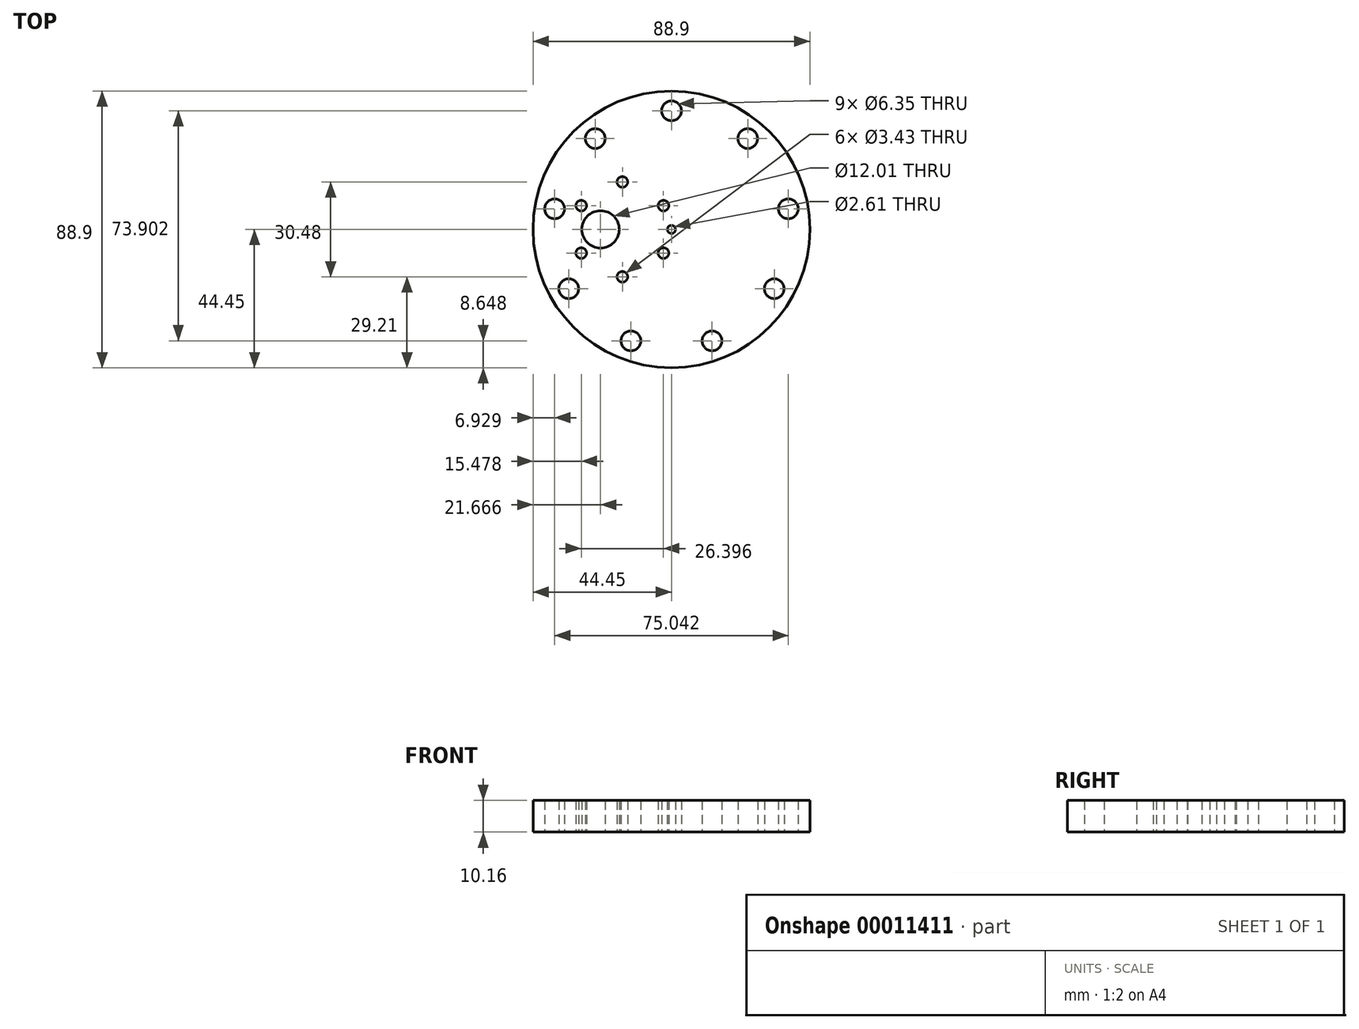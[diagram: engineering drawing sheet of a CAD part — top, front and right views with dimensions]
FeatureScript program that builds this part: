
annotation { "Feature Type Name" : "Feature", "Feature Type Description" : "" }
export const myFeature = defineFeature(function(context is Context, id is Id, definition is map)
    precondition{}
    {
        {
            var Q0;
            Q0=qCreatedBy(makeId("Top.planeOp"),FACE);
            var sketch = newSketch(context, id + "F0", { "sketchPlane" : qUnion([Q0])});
            skCircle(sketch, "E0", {"center": v(0, 0) * mm, "radius": 44.45 * mm});
            skCircle(sketch, "E1", {"center": v(0, 0) * mm, "radius": 15.77 * mm, "construction": true});
            skCircle(sketch, "E2", {"center": v(-15.77, 0) * mm, "radius": 18.44 * mm, "construction": true});
            skCircle(sketch, "E3", {"center": v(-15.77, 0) * mm, "radius": 15.24 * mm, "construction": true});
            skCircle(sketch, "E4", {"center": v(-22.78, 0) * mm, "radius": 6 * mm});
            skCircle(sketch, "E5", {"center": v(-15.77, 15.24) * mm, "radius": 1.71 * mm});
            skCircle(sketch, "E6.1.0", {"center": v(-28.97, 7.62) * mm, "radius": 1.71 * mm});
            skCircle(sketch, "E6.2.0", {"center": v(-28.97, -7.62) * mm, "radius": 1.71 * mm});
            skCircle(sketch, "E6.3.0", {"center": v(-15.77, -15.24) * mm, "radius": 1.71 * mm});
            skCircle(sketch, "E6.4.0", {"center": v(-2.58, -7.62) * mm, "radius": 1.71 * mm});
            skCircle(sketch, "E6.5.0", {"center": v(-2.58, 7.62) * mm, "radius": 1.71 * mm});
            skCircle(sketch, "E7", {"center": v(0, 0) * mm, "radius": 1.3 * mm});
            skCircle(sketch, "E8", {"center": v(0, 38.1) * mm, "radius": 3.18 * mm});
            skCircle(sketch, "E9.1.0", {"center": v(-24.5, 29.19) * mm, "radius": 3.18 * mm});
            skCircle(sketch, "E9.2.0", {"center": v(-37.52, 6.62) * mm, "radius": 3.18 * mm});
            skCircle(sketch, "E9.3.0", {"center": v(-33, -19.05) * mm, "radius": 3.18 * mm});
            skCircle(sketch, "E9.4.0", {"center": v(-13.03, -35.8) * mm, "radius": 3.18 * mm});
            skCircle(sketch, "E9.5.0", {"center": v(13.03, -35.8) * mm, "radius": 3.18 * mm});
            skCircle(sketch, "E9.6.0", {"center": v(33, -19.05) * mm, "radius": 3.18 * mm});
            skCircle(sketch, "E9.7.0", {"center": v(37.52, 6.62) * mm, "radius": 3.18 * mm});
            skCircle(sketch, "E9.8.0", {"center": v(24.5, 29.19) * mm, "radius": 3.18 * mm});
            skSolve(sketch);
        }
        {
            var Q0;
            Q0=makeQuery(id+"F0.imprint","IMPRINT",FACE,{"disambiguationData":[TD([[makeQuery(id+"F0.imprint","IMPRINT",EDGE,{"derivedFrom":sQuery(id+"F0.wireOp",EDGE,"E0")}),1.0]])]});
            extrude(context, id + "F1", {"entities" : qUnion([Q0]), "depth" : 10.16 * mm});
        }
    });
